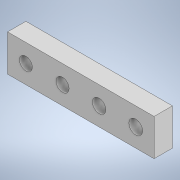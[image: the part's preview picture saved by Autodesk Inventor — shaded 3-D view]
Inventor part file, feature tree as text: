
AUTODESK INVENTOR PART (.ipt)
format: ipt  version: 2022 (Build 260153000, 153)  size: 115,712 bytes
history: native  units: mm
features: extrude x2, sketch x2, other x1
ambient origin geometry x8: Origin, YZ Plane, XZ Plane, XY Plane, X Axis, Y Axis, Z Axis, Center Point
bodies: Body1 (feature_tree)
feature tree (5):
  other  "ソリッド1"
  extrude  "押し出し1"  Depth=24.0mm
  extrude  "押し出し2"  Depth=6.0mm
  sketch  "スケッチ1"
  sketch  "スケッチ2"
